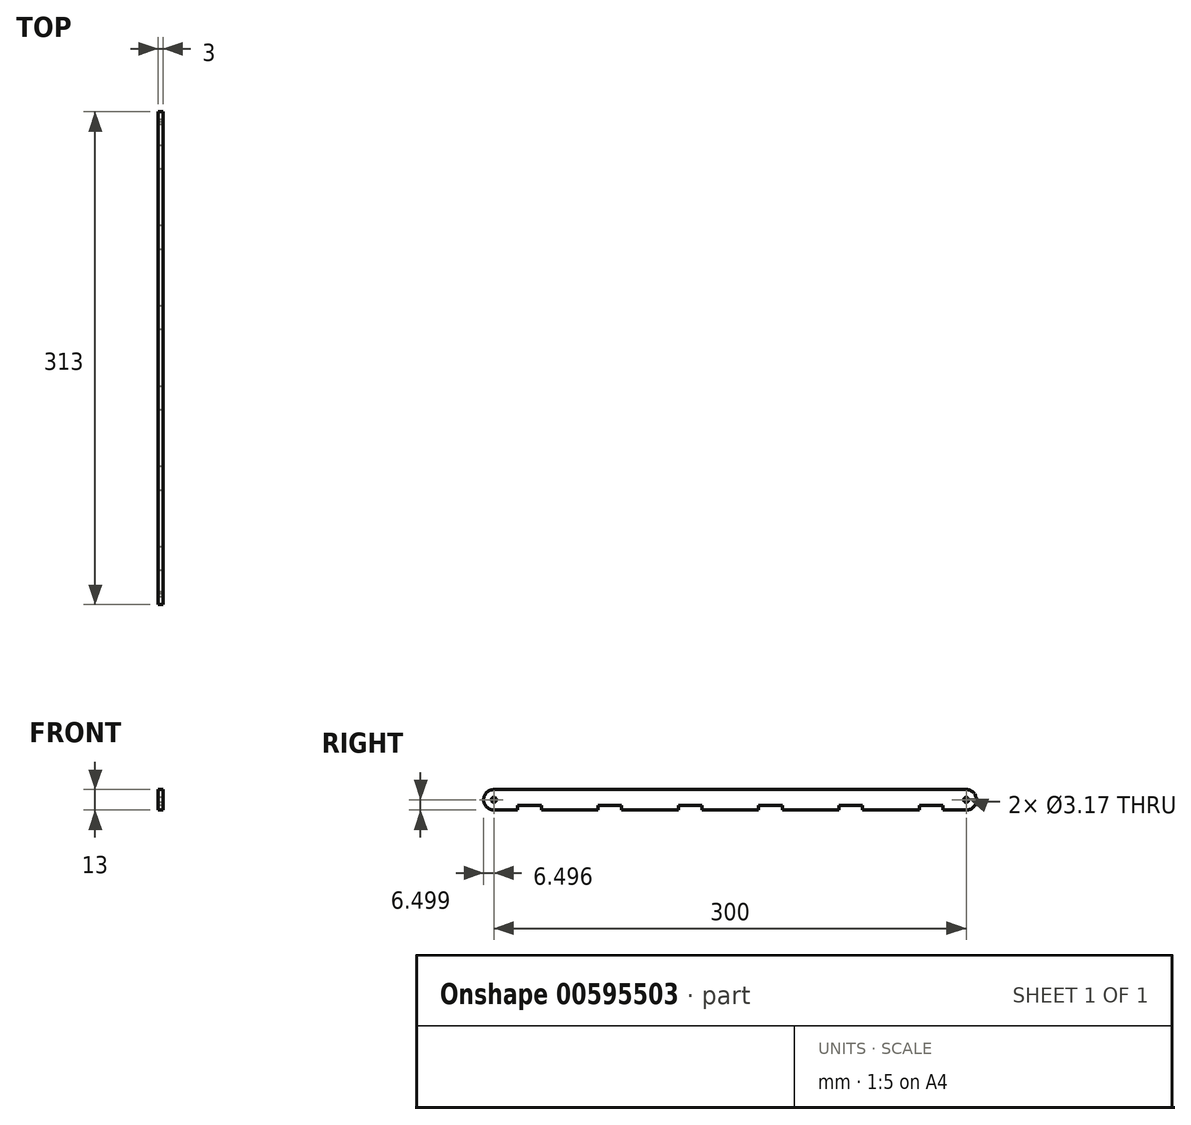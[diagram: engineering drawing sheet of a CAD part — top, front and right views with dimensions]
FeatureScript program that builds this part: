
annotation { "Feature Type Name" : "Feature", "Feature Type Description" : "" }
export const myFeature = defineFeature(function(context is Context, id is Id, definition is map)
    precondition{}
    {
        {
            var Q0;
            Q0=qCreatedBy(makeId("Right.planeOp"),FACE);
            var sketch = newSketch(context, id + "F0", { "sketchPlane" : qUnion([Q0])});
            skLineSegment(sketch, "E0.top", {"start": v(-0.13, 13) * mm, "end": v(-300.13, 13) * mm});
            skArc(sketch, "E1", {"start": v(-300.13, 13) * mm, "mid": v(-306.63, 6.43) * mm, "end": v(-300, 0) * mm});
            skArc(sketch, "E2", {"start": v(0, 0) * mm, "mid": v(6.37, 6.57) * mm, "end": v(-0.13, 13) * mm});
            skCircle(sketch, "E3", {"center": v(-300.13, 6.5) * mm, "radius": 1.59 * mm});
            skCircle(sketch, "E4", {"center": v(-0.13, 6.5) * mm, "radius": 1.59 * mm});
            skLineSegment(sketch, "E5", {"start": v(-300, 0) * mm, "end": v(-285, 0) * mm});
            skLineSegment(sketch, "E6", {"start": v(-285, 0) * mm, "end": v(-285, 3) * mm});
            skLineSegment(sketch, "E7", {"start": v(-285, 3) * mm, "end": v(-270, 3) * mm});
            skLineSegment(sketch, "E8", {"start": v(-270, 3) * mm, "end": v(-270, 0) * mm});
            skLineSegment(sketch, "E9", {"start": v(-270, 0) * mm, "end": v(-234, 0) * mm});
            skLineSegment(sketch, "E10", {"start": v(-234, 0) * mm, "end": v(-234, 3) * mm});
            skLineSegment(sketch, "E11", {"start": v(-234, 3) * mm, "end": v(-219, 3) * mm});
            skLineSegment(sketch, "E12", {"start": v(-219, 3) * mm, "end": v(-219, 0) * mm});
            skLineSegment(sketch, "E13", {"start": v(-219, 0) * mm, "end": v(-183, 0) * mm});
            skLineSegment(sketch, "E14", {"start": v(-183, 0) * mm, "end": v(-183, 3) * mm});
            skLineSegment(sketch, "E15", {"start": v(-183, 3) * mm, "end": v(-168, 3) * mm});
            skLineSegment(sketch, "E16", {"start": v(-168, 3) * mm, "end": v(-168, 0) * mm});
            skLineSegment(sketch, "E17", {"start": v(-168, 0) * mm, "end": v(-132, 0) * mm});
            skLineSegment(sketch, "E18", {"start": v(-132, 0) * mm, "end": v(-132, 3) * mm});
            skLineSegment(sketch, "E19", {"start": v(-132, 3) * mm, "end": v(-117, 3) * mm});
            skLineSegment(sketch, "E20", {"start": v(-117, 3) * mm, "end": v(-117, 0) * mm});
            skLineSegment(sketch, "E21", {"start": v(-117, 0) * mm, "end": v(-81, 0) * mm});
            skLineSegment(sketch, "E22", {"start": v(-81, 0) * mm, "end": v(-81, 3) * mm});
            skLineSegment(sketch, "E23", {"start": v(-81, 3) * mm, "end": v(-66, 3) * mm});
            skLineSegment(sketch, "E24", {"start": v(-66, 3) * mm, "end": v(-66, 0) * mm});
            skLineSegment(sketch, "E25", {"start": v(-66, 0) * mm, "end": v(-30, 0) * mm});
            skLineSegment(sketch, "E26", {"start": v(-30, 0) * mm, "end": v(-30, 3) * mm});
            skLineSegment(sketch, "E27", {"start": v(-30, 3) * mm, "end": v(-15, 3) * mm});
            skLineSegment(sketch, "E28", {"start": v(-15, 3) * mm, "end": v(-15, 0) * mm});
            skLineSegment(sketch, "E29", {"start": v(-15, 0) * mm, "end": v(0, 0) * mm});
            skSolve(sketch);
        }
        {
            var Q0;
            Q0=makeQuery(id+"F0.imprint","IMPRINT",FACE,{"disambiguationData":[TD([[makeQuery(id+"F0.imprint","IMPRINT",EDGE,{"derivedFrom":sQuery(id+"F0.wireOp",EDGE,"E0.top")}),1.0]])]});
            extrude(context, id + "F1", {"entities" : qUnion([Q0]), "depth" : 3 * mm, "offsetDistance" : 25 * mm});
        }
    });
